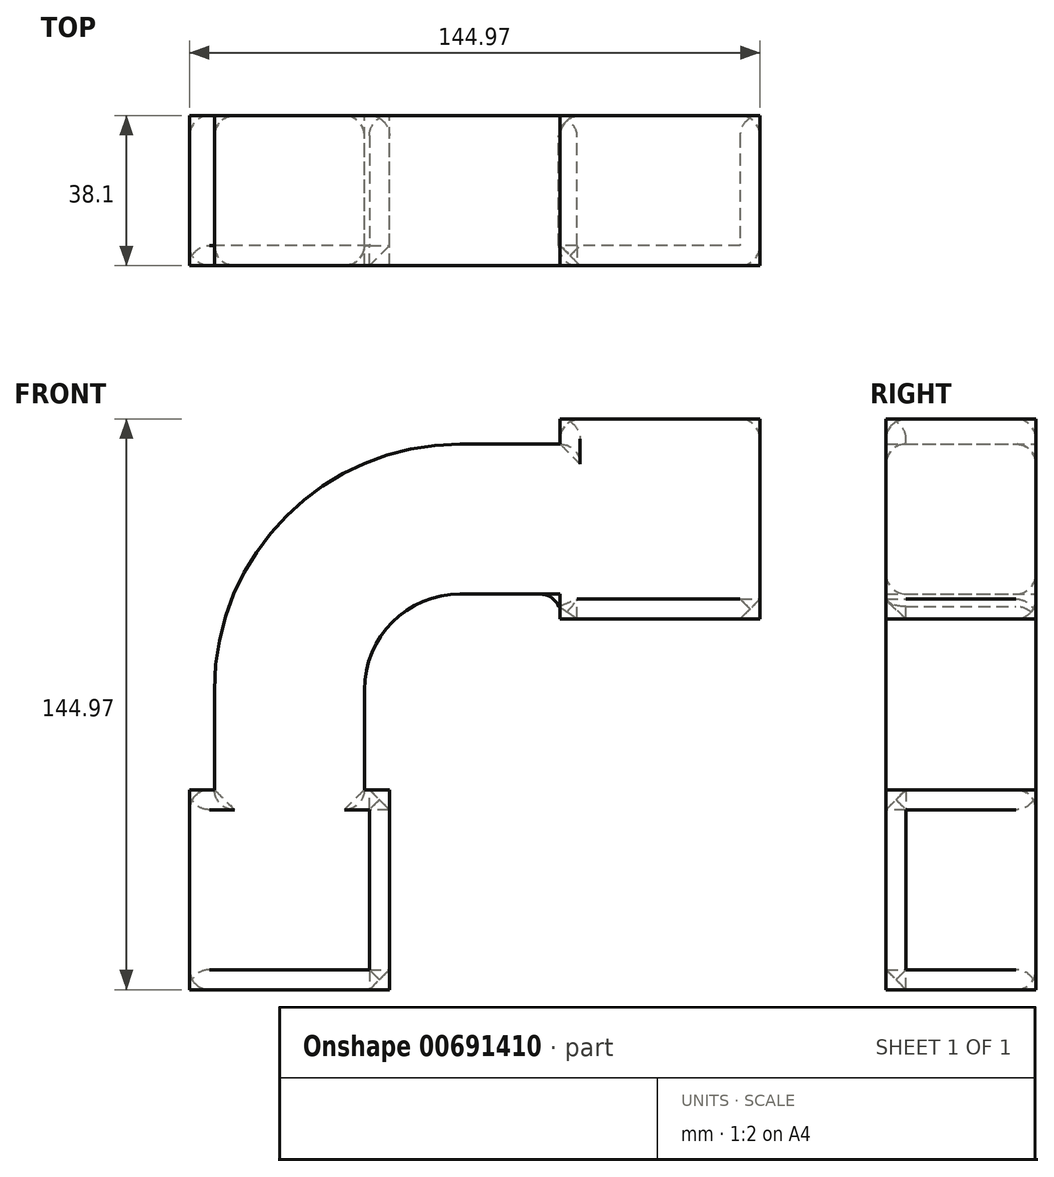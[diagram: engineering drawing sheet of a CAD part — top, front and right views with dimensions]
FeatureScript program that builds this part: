
annotation { "Feature Type Name" : "Feature", "Feature Type Description" : "" }
export const myFeature = defineFeature(function(context is Context, id is Id, definition is map)
    precondition{}
    {
        {
            var Q0;
            Q0=qCreatedBy(makeId("Front.planeOp"),FACE);
            var sketch = newSketch(context, id + "F0", { "sketchPlane" : qUnion([Q0])});
            skLineSegment(sketch, "E0.bottom", {"start": v(-25.4, 25.4) * mm, "end": v(25.4, 25.4) * mm});
            skLineSegment(sketch, "E0.top", {"start": v(-25.4, -25.4) * mm, "end": v(25.4, -25.4) * mm});
            skLineSegment(sketch, "E0.left", {"start": v(-25.4, 25.4) * mm, "end": v(-25.4, -25.4) * mm});
            skLineSegment(sketch, "E0.right", {"start": v(25.4, 25.4) * mm, "end": v(25.4, -25.4) * mm});
            skPoint(sketch, "E0.middle", {"position": v(0, 0) * mm});
            skLineSegment(sketch, "E1.bottom", {"start": v(68.77, 68.77) * mm, "end": v(119.57, 68.77) * mm});
            skLineSegment(sketch, "E1.top", {"start": v(68.77, 119.57) * mm, "end": v(119.57, 119.57) * mm});
            skLineSegment(sketch, "E1.left", {"start": v(68.77, 68.77) * mm, "end": v(68.77, 119.57) * mm});
            skLineSegment(sketch, "E1.right", {"start": v(119.57, 68.77) * mm, "end": v(119.57, 119.57) * mm});
            skLineSegment(sketch, "E2.0", {"start": v(43.37, 113.22) * mm, "end": v(68.77, 113.22) * mm});
            skArc(sketch, "E2.1", {"start": v(-19.05, 50.8) * mm, "mid": v(-0.77, 94.94) * mm, "end": v(43.37, 113.22) * mm});
            skLineSegment(sketch, "E2.2", {"start": v(-19.05, 25.4) * mm, "end": v(-19.05, 50.8) * mm});
            skLineSegment(sketch, "E3.0", {"start": v(43.37, 75.12) * mm, "end": v(68.77, 75.12) * mm});
            skArc(sketch, "E3.1", {"start": v(19.05, 50.8) * mm, "mid": v(26.17, 68) * mm, "end": v(43.37, 75.12) * mm});
            skLineSegment(sketch, "E3.2", {"start": v(19.05, 25.4) * mm, "end": v(19.05, 50.8) * mm});
            skSolve(sketch);
        }
        {
            var Q0;
            {var subQ0=sQuery(id+"F0.wireOp",EDGE,"E2.0");Q0=makeQuery(id+"F0.imprint","IMPRINT",FACE,{"disambiguationData":[TD([[makeQuery(id+"F0.imprint","IMPRINT",EDGE,{"derivedFrom":subQ0}),-1.0]])]});}
            var Q1;
            Q1=makeQuery(id+"F0.imprint","IMPRINT",FACE,{"disambiguationData":[TD([[makeQuery(id+"F0.imprint","IMPRINT",EDGE,{"derivedFrom":sQuery(id+"F0.wireOp",EDGE,"E0.top")}),1.0]])]});
            var Q2;
            {var subQ3=sQuery(id+"F0.wireOp",EDGE,"E1.bottom");Q2=makeQuery(id+"F0.imprint","IMPRINT",FACE,{"disambiguationData":[TD([[makeQuery(id+"F0.imprint","IMPRINT",EDGE,{"derivedFrom":subQ3}),1.0]])]});}
            extrude(context, id + "F1", {"entities" : qUnion([Q0, Q1, Q2]), "endBound" : BoundingType.SYMMETRIC, "depth" : 38.1 * mm, "offsetDistance" : 25.4 * mm});
        }
        {
            var Q0;
            Q0=makeQuery(id+"F1.opExtrude","SWEPT_FACE",FACE,{"disambiguationData":[OSD([sQuery(id+"F0.wireOp",EDGE,"E0.left")])]});
            var Q1;
            Q1=makeQuery(id+"F1.opExtrude","CAP_FACE",FACE,{"disambiguationData":[OSD([sQuery(id+"F0.wireOp",EDGE,"E0.bottom"),sQuery(id+"F0.wireOp",EDGE,"E0.top"),sQuery(id+"F0.wireOp",EDGE,"E0.left"),sQuery(id+"F0.wireOp",EDGE,"E0.right"),sQuery(id+"F0.wireOp",EDGE,"E1.bottom"),sQuery(id+"F0.wireOp",EDGE,"E1.top"),sQuery(id+"F0.wireOp",EDGE,"E1.left"),sQuery(id+"F0.wireOp",EDGE,"E1.right"),sQuery(id+"F0.wireOp",EDGE,"E2.0"),sQuery(id+"F0.wireOp",EDGE,"E2.1"),sQuery(id+"F0.wireOp",EDGE,"E2.2"),sQuery(id+"F0.wireOp",EDGE,"E3.0"),sQuery(id+"F0.wireOp",EDGE,"E3.1"),sQuery(id+"F0.wireOp",EDGE,"E3.2")])],"isStart":true});
            var Q2;
            Q2=makeQuery(id+"F1.opExtrude","SWEPT_FACE",FACE,{"disambiguationData":[OSD([sQuery(id+"F0.wireOp",EDGE,"E1.top")])]});
            var Q3;
            Q3=makeQuery(id+"F1.opExtrude","SWEPT_EDGE",EDGE,{"disambiguationData":[OSD([sQuery(id+"F0.wireOp",EDGE,"E2.0"),sQuery(id+"F0.wireOp",EDGE,"E2.1")])]});
            var Q4;
            Q4=makeQuery(id+"F1.opExtrude","SWEPT_FACE",FACE,{"disambiguationData":[OSD([sQuery(id+"F0.wireOp",EDGE,"E2.1")])]});
            var Q5;
            Q5=makeQuery(id+"F1.opExtrude","SWEPT_FACE",FACE,{"disambiguationData":[OSD([sQuery(id+"F0.wireOp",EDGE,"E3.0")])]});
            var Q6;
            Q6=makeQuery(id+"F1.opExtrude","CAP_EDGE",EDGE,{"disambiguationData":[OSD([sQuery(id+"F0.wireOp",EDGE,"E1.right")])],"isStart":false});
            fillet(context, id + "F2", {"entities" : qUnion([Q0, Q1, Q2, Q3, Q4, Q5, Q6]), "radius" : 5.08 * mm, "tangentPropagation" : true, "allowEdgeOverflow" : false});
        }
        {
            var Q0;
            Q0=makeQuery(id+"F1.opExtrude","CAP_FACE",FACE,{"disambiguationData":[OSD([sQuery(id+"F0.wireOp",EDGE,"E0.bottom"),sQuery(id+"F0.wireOp",EDGE,"E0.top"),sQuery(id+"F0.wireOp",EDGE,"E0.left"),sQuery(id+"F0.wireOp",EDGE,"E0.right"),sQuery(id+"F0.wireOp",EDGE,"E1.bottom"),sQuery(id+"F0.wireOp",EDGE,"E1.top"),sQuery(id+"F0.wireOp",EDGE,"E1.left"),sQuery(id+"F0.wireOp",EDGE,"E1.right"),sQuery(id+"F0.wireOp",EDGE,"E2.0"),sQuery(id+"F0.wireOp",EDGE,"E2.1"),sQuery(id+"F0.wireOp",EDGE,"E2.2"),sQuery(id+"F0.wireOp",EDGE,"E3.0"),sQuery(id+"F0.wireOp",EDGE,"E3.1"),sQuery(id+"F0.wireOp",EDGE,"E3.2")])],"isStart":true});
            var Q1;
            Q1=makeQuery(id+"F1.opExtrude","SWEPT_FACE",FACE,{"disambiguationData":[OSD([sQuery(id+"F0.wireOp",EDGE,"E2.1")])]});
            var Q2;
            Q2=makeQuery(id+"F1.opExtrude","SWEPT_FACE",FACE,{"disambiguationData":[OSD([sQuery(id+"F0.wireOp",EDGE,"E1.top")])]});
            var Q3;
            Q3=makeQuery(id+"F1.opExtrude","SWEPT_FACE",FACE,{"disambiguationData":[OSD([sQuery(id+"F0.wireOp",EDGE,"E0.left")])]});
            var Q4;
            Q4=makeQuery(id+"F1.opExtrude","SWEPT_FACE",FACE,{"disambiguationData":[OSD([sQuery(id+"F0.wireOp",EDGE,"E1.right")])]});
            var Q5;
            Q5=makeQuery(id+"F1.opExtrude","CAP_FACE",FACE,{"disambiguationData":[OSD([sQuery(id+"F0.wireOp",EDGE,"E0.bottom"),sQuery(id+"F0.wireOp",EDGE,"E0.top"),sQuery(id+"F0.wireOp",EDGE,"E0.left"),sQuery(id+"F0.wireOp",EDGE,"E0.right"),sQuery(id+"F0.wireOp",EDGE,"E1.bottom"),sQuery(id+"F0.wireOp",EDGE,"E1.top"),sQuery(id+"F0.wireOp",EDGE,"E1.left"),sQuery(id+"F0.wireOp",EDGE,"E1.right"),sQuery(id+"F0.wireOp",EDGE,"E2.0"),sQuery(id+"F0.wireOp",EDGE,"E2.1"),sQuery(id+"F0.wireOp",EDGE,"E2.2"),sQuery(id+"F0.wireOp",EDGE,"E3.0"),sQuery(id+"F0.wireOp",EDGE,"E3.1"),sQuery(id+"F0.wireOp",EDGE,"E3.2")])],"isStart":false});
            var Q6;
            Q6=makeQuery(id+"F1.opExtrude","SWEPT_FACE",FACE,{"disambiguationData":[OSD([sQuery(id+"F0.wireOp",EDGE,"E0.right")])]});
            var Q7;
            Q7=makeQuery(id+"F1.opExtrude","SWEPT_FACE",FACE,{"disambiguationData":[OSD([sQuery(id+"F0.wireOp",EDGE,"E0.top")])]});
            var Q8;
            Q8=makeQuery(id+"F1.opExtrude","SWEPT_FACE",FACE,{"disambiguationData":[OSD([sQuery(id+"F0.wireOp",EDGE,"E3.1")])]});
            var Q9;
            Q9=makeQuery(id+"F1.opExtrude","SWEPT_FACE",FACE,{"disambiguationData":[OSD([sQuery(id+"F0.wireOp",EDGE,"E3.0")])]});
            chamfer(context, id + "F3", {"entities" : qUnion([Q0, Q1, Q2, Q3, Q4, Q5, Q6, Q7, Q8, Q9]), "width" : 5.08 * mm, "tangentPropagation" : true});
        }
        {
            var Q0;
            Q0=makeQuery(id+"F0.imprint","IMPRINT",FACE,{"disambiguationData":[TD([[makeQuery(id+"F0.imprint","IMPRINT",EDGE,{"derivedFrom":sQuery(id+"F0.wireOp",EDGE,"E0.top")}),1.0]])]});
            var Q1;
            {var subQ3=sQuery(id+"F0.wireOp",EDGE,"E1.bottom");Q1=makeQuery(id+"F0.imprint","IMPRINT",FACE,{"disambiguationData":[TD([[makeQuery(id+"F0.imprint","IMPRINT",EDGE,{"derivedFrom":subQ3}),1.0]])]});}
            var Q2;
            {var subQ0=sQuery(id+"F0.wireOp",EDGE,"E2.0");Q2=makeQuery(id+"F0.imprint","IMPRINT",FACE,{"disambiguationData":[TD([[makeQuery(id+"F0.imprint","IMPRINT",EDGE,{"derivedFrom":subQ0}),-1.0]])]});}
            extrude(context, id + "F4", {"entities" : qUnion([Q0, Q1, Q2]), "endBound" : BoundingType.SYMMETRIC, "depth" : 38.1 * mm, "offsetDistance" : 25.4 * mm});
        }
    });
